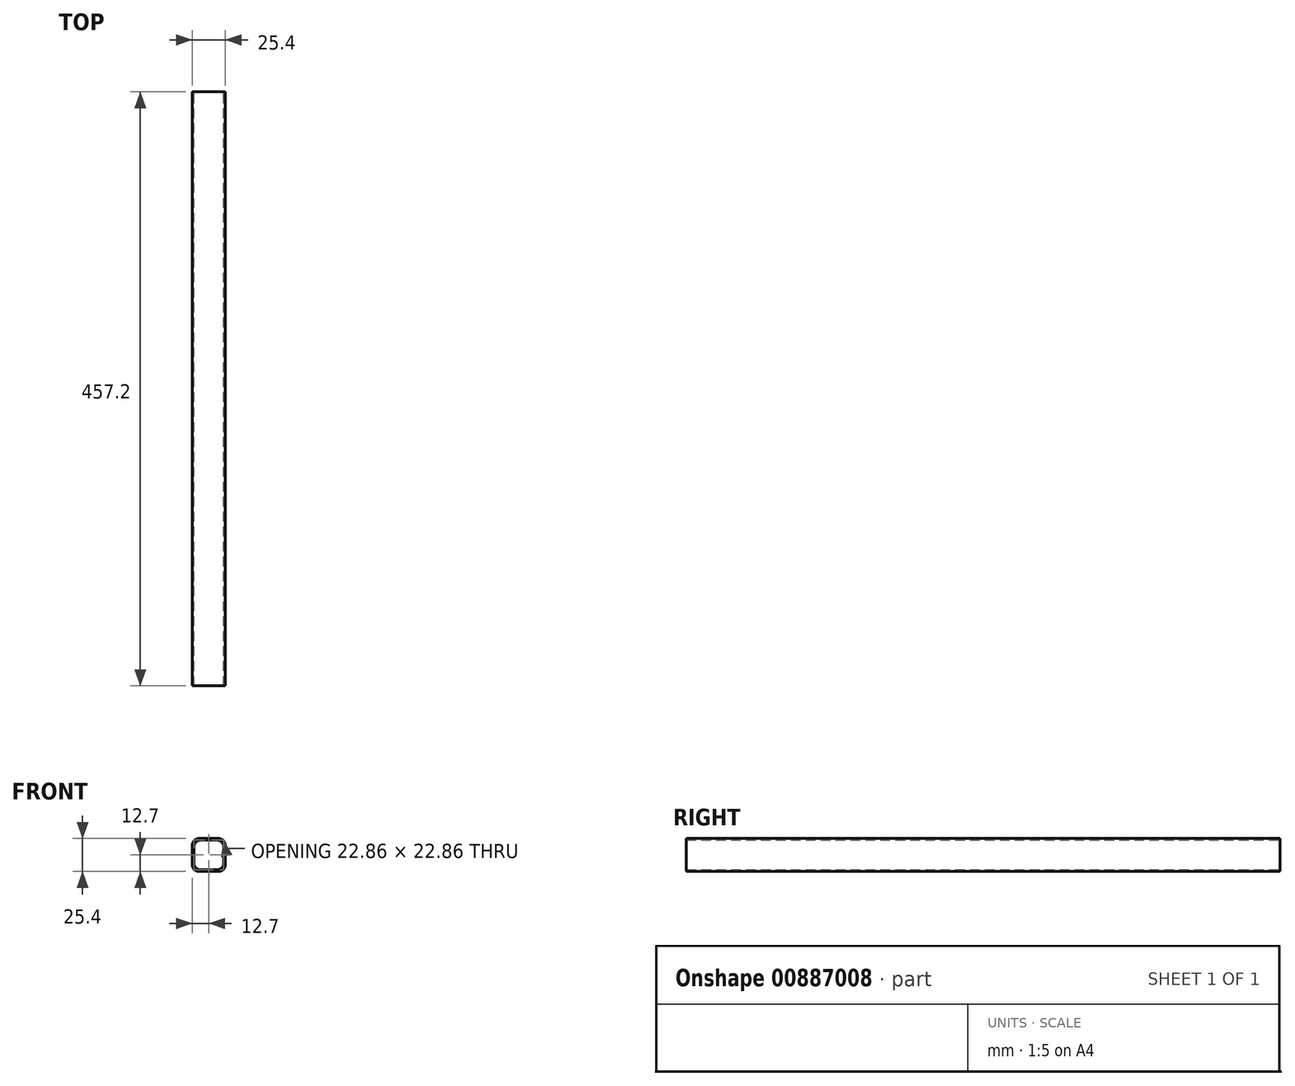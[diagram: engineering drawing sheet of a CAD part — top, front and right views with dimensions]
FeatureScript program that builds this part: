
annotation { "Feature Type Name" : "Feature", "Feature Type Description" : "" }
export const myFeature = defineFeature(function(context is Context, id is Id, definition is map)
    precondition{}
    {
        {
            var Q0;
            Q0=qCreatedBy(makeId("Front.planeOp"),FACE);
            var sketch = newSketch(context, id + "F0", { "sketchPlane" : qUnion([Q0])});
            skLineSegment(sketch, "E0.bottom", {"start": v(-12.7, 12.7) * mm, "end": v(12.7, 12.7) * mm});
            skLineSegment(sketch, "E0.top", {"start": v(-12.7, -12.7) * mm, "end": v(12.7, -12.7) * mm});
            skLineSegment(sketch, "E0.left", {"start": v(-12.7, 12.7) * mm, "end": v(-12.7, -12.7) * mm});
            skLineSegment(sketch, "E0.right", {"start": v(12.7, 12.7) * mm, "end": v(12.7, -12.7) * mm});
            skPoint(sketch, "E0.middle", {"position": v(0, 0) * mm});
            skLineSegment(sketch, "E1.bottom", {"start": v(-11.43, 11.43) * mm, "end": v(11.43, 11.43) * mm});
            skLineSegment(sketch, "E1.top", {"start": v(-11.43, -11.43) * mm, "end": v(11.43, -11.43) * mm});
            skLineSegment(sketch, "E1.left", {"start": v(-11.43, 11.43) * mm, "end": v(-11.43, -11.43) * mm});
            skLineSegment(sketch, "E1.right", {"start": v(11.43, 11.43) * mm, "end": v(11.43, -11.43) * mm});
            skSolve(sketch);
        }
        {
            var Q0;
            Q0 = qSketchRegion(id + "F0", true);
            extrude(context, id + "F1", {"entities" : qUnion([Q0]), "endBound" : BoundingType.SYMMETRIC, "depth" : 457.2 * mm, "offsetDistance" : 25.4 * mm});
        }
        {
            var Q0;
            Q0=makeQuery(id+"F1.opExtrude","SWEPT_EDGE",EDGE,{"disambiguationData":[OSD([sQuery(id+"F0.wireOp",EDGE,"E1.bottom"),sQuery(id+"F0.wireOp",EDGE,"E1.left")])]});
            var Q1;
            Q1=makeQuery(id+"F1.opExtrude","SWEPT_EDGE",EDGE,{"disambiguationData":[OSD([sQuery(id+"F0.wireOp",EDGE,"E1.bottom"),sQuery(id+"F0.wireOp",EDGE,"E1.right")])]});
            var Q2;
            Q2=makeQuery(id+"F1.opExtrude","SWEPT_EDGE",EDGE,{"disambiguationData":[OSD([sQuery(id+"F0.wireOp",EDGE,"E1.top"),sQuery(id+"F0.wireOp",EDGE,"E1.left")])]});
            var Q3;
            Q3=makeQuery(id+"F1.opExtrude","SWEPT_EDGE",EDGE,{"disambiguationData":[OSD([sQuery(id+"F0.wireOp",EDGE,"E1.top"),sQuery(id+"F0.wireOp",EDGE,"E1.right")])]});
            var Q4;
            Q4=makeQuery(id+"F1.opExtrude","SWEPT_EDGE",EDGE,{"disambiguationData":[OSD([sQuery(id+"F0.wireOp",EDGE,"E0.bottom"),sQuery(id+"F0.wireOp",EDGE,"E0.left")])]});
            var Q5;
            Q5=makeQuery(id+"F1.opExtrude","SWEPT_EDGE",EDGE,{"disambiguationData":[OSD([sQuery(id+"F0.wireOp",EDGE,"E0.bottom"),sQuery(id+"F0.wireOp",EDGE,"E0.right")])]});
            var Q6;
            Q6=makeQuery(id+"F1.opExtrude","SWEPT_EDGE",EDGE,{"disambiguationData":[OSD([sQuery(id+"F0.wireOp",EDGE,"E0.top"),sQuery(id+"F0.wireOp",EDGE,"E0.left")])]});
            var Q7;
            Q7=makeQuery(id+"F1.opExtrude","SWEPT_EDGE",EDGE,{"disambiguationData":[OSD([sQuery(id+"F0.wireOp",EDGE,"E0.top"),sQuery(id+"F0.wireOp",EDGE,"E0.right")])]});
            fillet(context, id + "F2", {"entities" : qUnion([Q0, Q1, Q2, Q3, Q4, Q5, Q6, Q7]), "radius" : 5.08 * mm, "tangentPropagation" : true, "allowEdgeOverflow" : false});
        }
    });
